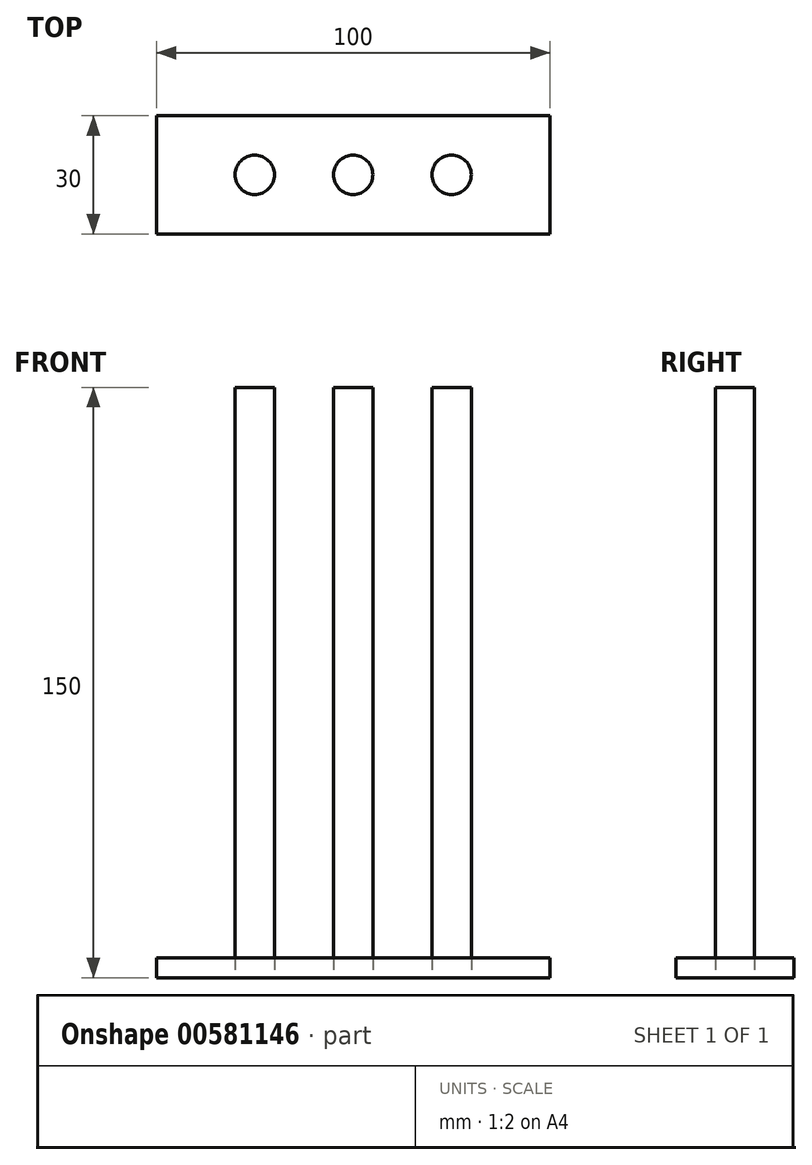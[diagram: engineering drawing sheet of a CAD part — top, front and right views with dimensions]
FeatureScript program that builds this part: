
annotation { "Feature Type Name" : "Feature", "Feature Type Description" : "" }
export const myFeature = defineFeature(function(context is Context, id is Id, definition is map)
    precondition{}
    {
        {
            var Q0;
            Q0=qCreatedBy(makeId("Top.planeOp"),FACE);
            var sketch = newSketch(context, id + "F0", { "sketchPlane" : qUnion([Q0])});
            skLineSegment(sketch, "E0.bottom", {"start": v(-50, 15) * mm, "end": v(50, 15) * mm});
            skLineSegment(sketch, "E0.top", {"start": v(-50, -15) * mm, "end": v(50, -15) * mm});
            skLineSegment(sketch, "E0.left", {"start": v(-50, 15) * mm, "end": v(-50, -15) * mm});
            skLineSegment(sketch, "E0.right", {"start": v(50, 15) * mm, "end": v(50, -15) * mm});
            skPoint(sketch, "E0.middle", {"position": v(0, 0) * mm});
            skCircle(sketch, "E1", {"center": v(0, 0) * mm, "radius": 5 * mm});
            skCircle(sketch, "E2", {"center": v(-25, 0) * mm, "radius": 5 * mm});
            skCircle(sketch, "E3", {"center": v(25, 0) * mm, "radius": 5 * mm});
            skLineSegment(sketch, "E4", {"start": v(0, 15) * mm, "end": v(0, -15) * mm, "construction": true});
            skPoint(sketch, "E5.orphan", {"position": v(-50, 0) * mm});
            skSolve(sketch);
        }
        {
            var Q0;
            Q0=makeQuery(id+"F0.imprint","IMPRINT",FACE,{"disambiguationData":[TD([[makeQuery(id+"F0.imprint","IMPRINT",EDGE,{"derivedFrom":sQuery(id+"F0.wireOp",EDGE,"E0.bottom")}),-1.0]])]});
            var Q1;
            Q1=makeQuery(id+"F0.imprint","IMPRINT",FACE,{"disambiguationData":[TD([[makeQuery(id+"F0.imprint","IMPRINT",EDGE,{"derivedFrom":sQuery(id+"F0.wireOp",EDGE,"E2")}),1.0]])]});
            var Q2;
            Q2=makeQuery(id+"F0.imprint","IMPRINT",FACE,{"disambiguationData":[TD([[makeQuery(id+"F0.imprint","IMPRINT",EDGE,{"derivedFrom":sQuery(id+"F0.wireOp",EDGE,"E1")}),1.0]])]});
            var Q3;
            Q3=makeQuery(id+"F0.imprint","IMPRINT",FACE,{"disambiguationData":[TD([[makeQuery(id+"F0.imprint","IMPRINT",EDGE,{"derivedFrom":sQuery(id+"F0.wireOp",EDGE,"E3")}),1.0]])]});
            extrude(context, id + "F1", {"entities" : qUnion([Q0, Q1, Q2, Q3]), "depth" : 5 * mm, "offsetDistance" : 25 * mm});
        }
        {
            var Q0;
            Q0=makeQuery(id+"F0.imprint","IMPRINT",FACE,{"disambiguationData":[TD([[makeQuery(id+"F0.imprint","IMPRINT",EDGE,{"derivedFrom":sQuery(id+"F0.wireOp",EDGE,"E2")}),1.0]])]});
            var Q1;
            Q1=makeQuery(id+"F0.imprint","IMPRINT",FACE,{"disambiguationData":[TD([[makeQuery(id+"F0.imprint","IMPRINT",EDGE,{"derivedFrom":sQuery(id+"F0.wireOp",EDGE,"E1")}),1.0]])]});
            var Q2;
            Q2=makeQuery(id+"F0.imprint","IMPRINT",FACE,{"disambiguationData":[TD([[makeQuery(id+"F0.imprint","IMPRINT",EDGE,{"derivedFrom":sQuery(id+"F0.wireOp",EDGE,"E3")}),1.0]])]});
            extrude(context, id + "F2", {"entities" : qUnion([Q0, Q1, Q2]), "depth" : 150 * mm, "offsetDistance" : 25 * mm});
        }
    });
